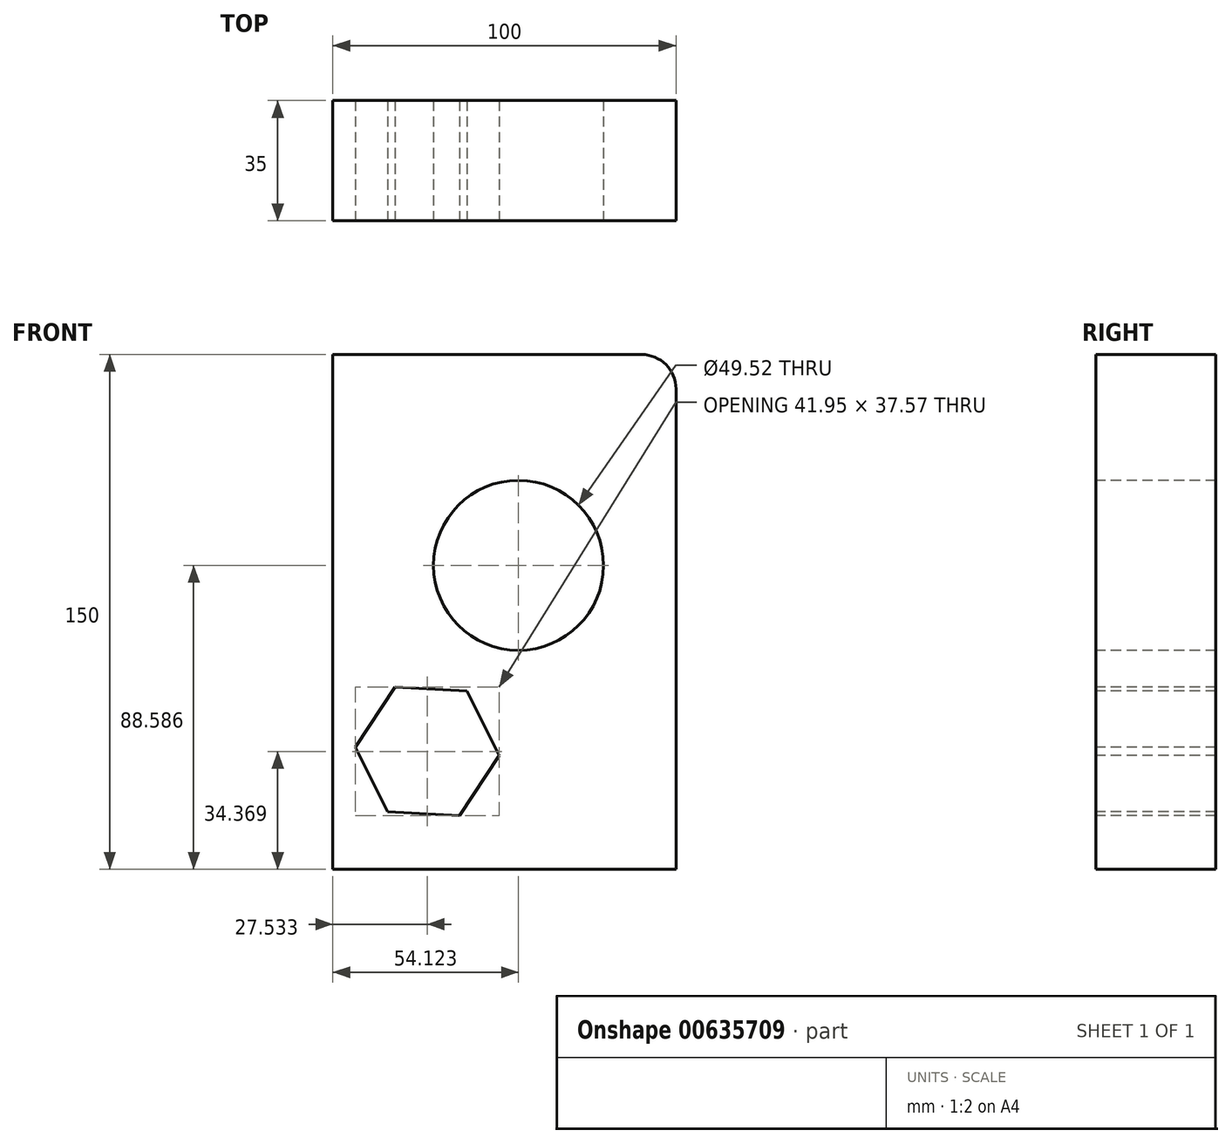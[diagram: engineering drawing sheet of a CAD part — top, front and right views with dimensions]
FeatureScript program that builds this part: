
annotation { "Feature Type Name" : "Feature", "Feature Type Description" : "" }
export const myFeature = defineFeature(function(context is Context, id is Id, definition is map)
    precondition{}
    {
        {
            var Q0;
            Q0=qCreatedBy(makeId("Front.planeOp"),FACE);
            var sketch = newSketch(context, id + "F0", { "sketchPlane" : qUnion([Q0])});
            skLineSegment(sketch, "E0.bottom", {"start": v(-48.08, 99.97) * mm, "end": v(51.92, 99.97) * mm});
            skLineSegment(sketch, "E0.top", {"start": v(-48.08, -50.03) * mm, "end": v(51.92, -50.03) * mm});
            skLineSegment(sketch, "E0.left", {"start": v(-48.08, 99.97) * mm, "end": v(-48.08, -50.03) * mm});
            skLineSegment(sketch, "E0.right", {"start": v(51.92, 99.97) * mm, "end": v(51.92, -50.03) * mm});
            skSolve(sketch);
        }
        {
            var Q0;
            Q0=makeQuery(id+"F0.imprint","IMPRINT",FACE,{"disambiguationData":[TD([[makeQuery(id+"F0.imprint","IMPRINT",EDGE,{"derivedFrom":sQuery(id+"F0.wireOp",EDGE,"E0.bottom")}),-1.0]])]});
            extrude(context, id + "F1", {"entities" : qUnion([Q0]), "depth" : 35 * mm, "offsetDistance" : 25 * mm});
        }
        {
            var Q0;
            Q0=makeQuery(id+"F1.opExtrude","CAP_FACE",FACE,{"disambiguationData":[OSD([sQuery(id+"F0.wireOp",EDGE,"E0.bottom"),sQuery(id+"F0.wireOp",EDGE,"E0.top"),sQuery(id+"F0.wireOp",EDGE,"E0.left"),sQuery(id+"F0.wireOp",EDGE,"E0.right")])],"isStart":false});
            var sketch = newSketch(context, id + "F2", { "sketchPlane" : qUnion([Q0])});
            skCircle(sketch, "E1", {"center": v(6.04, 38.56) * mm, "radius": 24.76 * mm});
            skCircle(sketch, "E2.cCircle", {"center": v(-20.55, -15.66) * mm, "radius": 18.2 * mm, "construction": true});
            skLineSegment(sketch, "E2.0", {"start": v(0.43, -16.9) * mm, "end": v(-11.13, -34.45) * mm});
            skLineSegment(sketch, "E2.1", {"start": v(-11.13, -34.45) * mm, "end": v(-32.11, -33.2) * mm});
            skLineSegment(sketch, "E2.2", {"start": v(-32.11, -33.2) * mm, "end": v(-41.52, -14.42) * mm});
            skLineSegment(sketch, "E2.3", {"start": v(-41.52, -14.42) * mm, "end": v(-29.96, 3.13) * mm});
            skLineSegment(sketch, "E2.4", {"start": v(-29.96, 3.13) * mm, "end": v(-8.98, 1.88) * mm});
            skLineSegment(sketch, "E2.5", {"start": v(-8.98, 1.88) * mm, "end": v(0.43, -16.9) * mm});
            skPoint(sketch, "E2.0.midPoint", {"position": v(-5.35, -25.68) * mm});
            skSolve(sketch);
        }
        {
            var Q0;
            Q0 = qSketchRegion(id + "F2", true);
            extrude(context, id + "F3", {"entities" : qUnion([Q0]), "operationType" : NewBodyOperationType.REMOVE, "oppositeDirection" : true, "depth" : 93 * mm, "offsetDistance" : 25 * mm});
        }
        {
            var Q0;
            Q0=makeQuery(id+"F1.opExtrude","SWEPT_EDGE",EDGE,{"disambiguationData":[OSD([sQuery(id+"F0.wireOp",EDGE,"E0.bottom"),sQuery(id+"F0.wireOp",EDGE,"E0.right")])]});
            fillet(context, id + "F4", {"entities" : qUnion([Q0]), "radius" : 10 * mm, "tangentPropagation" : true, "allowEdgeOverflow" : false});
        }
    });
